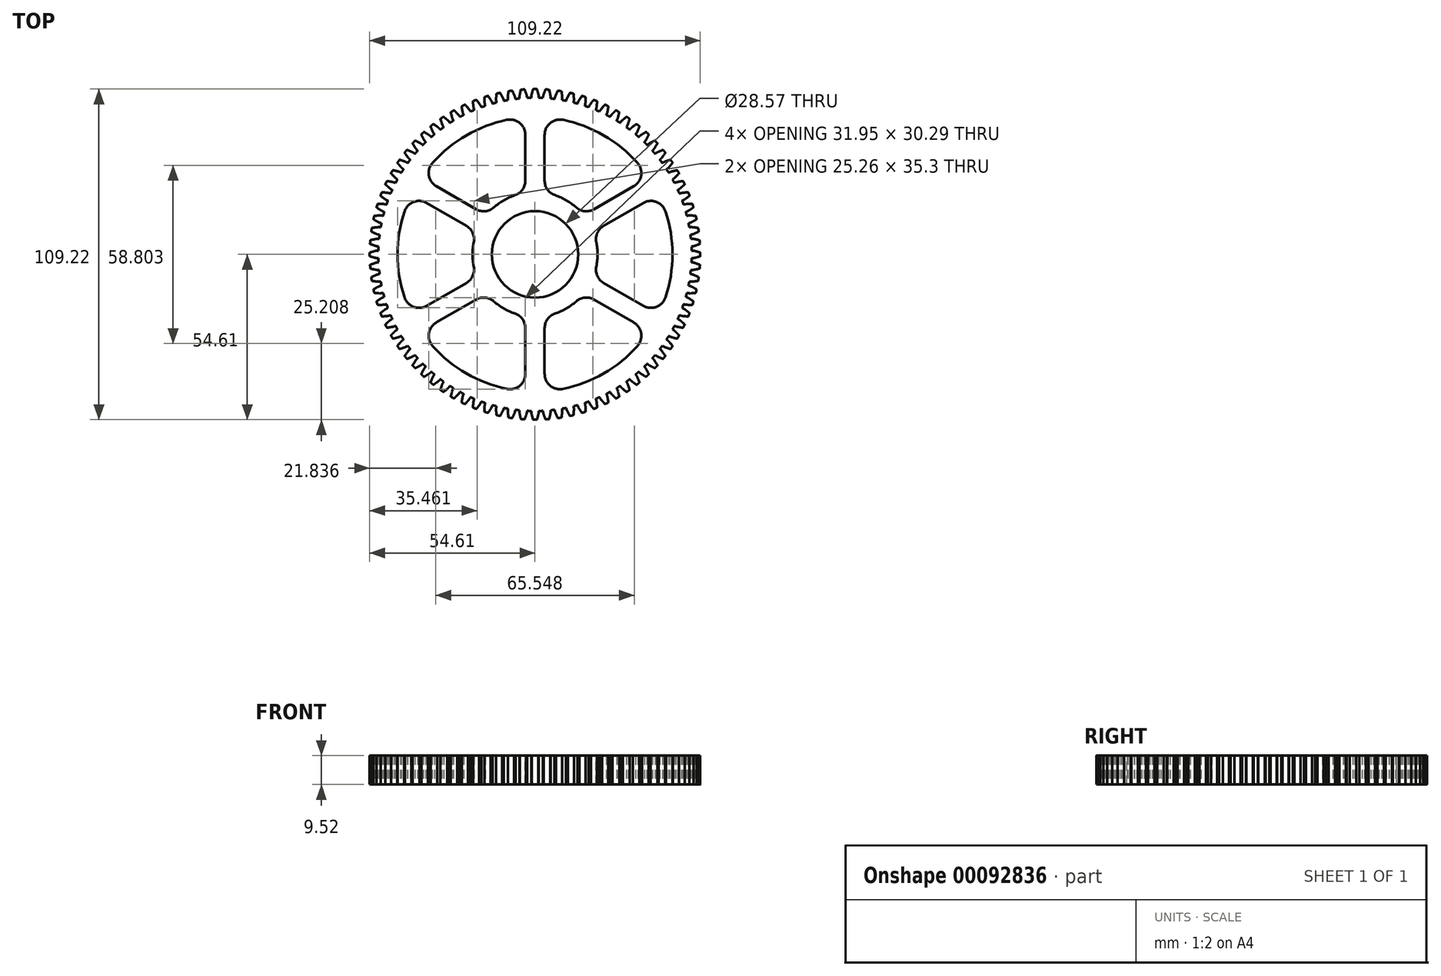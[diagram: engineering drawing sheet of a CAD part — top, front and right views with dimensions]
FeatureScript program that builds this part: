
annotation { "Feature Type Name" : "Feature", "Feature Type Description" : "" }
export const myFeature = defineFeature(function(context is Context, id is Id, definition is map)
    precondition{}
    {
        {
            var Q0;
            Q0=qCreatedBy(makeId("Top.planeOp"),FACE);
            var sketch = newSketch(context, id + "F0", { "sketchPlane" : qUnion([Q0])});
            skArc(sketch, "E0", {"start": v(1.25, 51.74) * mm, "mid": v(0, 51.75) * mm, "end": v(-1.25, 51.74) * mm});
            skArc(sketch, "E1", {"start": v(-1.25, -51.74) * mm, "mid": v(51.74, -1.25) * mm, "end": v(1.25, 51.74) * mm});
            skArc(sketch, "E2", {"start": v(-1.05, 53.12) * mm, "mid": v(-1.2, 52.43) * mm, "end": v(-1.25, 51.74) * mm});
            skArc(sketch, "E3", {"start": v(-0.67, 54.46) * mm, "mid": v(-0.86, 53.79) * mm, "end": v(-1.05, 53.12) * mm});
            skArc(sketch, "E4", {"start": v(-0.48, 54.6) * mm, "mid": v(-0.6, 54.57) * mm, "end": v(-0.67, 54.46) * mm});
            skArc(sketch, "E5", {"start": v(1.25, 51.74) * mm, "mid": v(1.2, 52.43) * mm, "end": v(1.05, 53.12) * mm});
            skArc(sketch, "E6", {"start": v(1.05, 53.12) * mm, "mid": v(0.86, 53.79) * mm, "end": v(0.67, 54.46) * mm});
            skArc(sketch, "E7", {"start": v(0.48, 54.6) * mm, "mid": v(0, 54.61) * mm, "end": v(-0.48, 54.6) * mm});
            skArc(sketch, "E8", {"start": v(0.67, 54.46) * mm, "mid": v(0.6, 54.57) * mm, "end": v(0.48, 54.6) * mm});
            skArc(sketch, "E9", {"start": v(-1.25, 51.74) * mm, "mid": v(-51.75, 0) * mm, "end": v(-1.25, -51.74) * mm});
            skSolve(sketch);
        }
        {
            var Q0;
            Q0=makeQuery(id+"F0.imprint","IMPRINT",FACE,{"disambiguationData":[TD([[makeQuery(id+"F0.imprint","IMPRINT",EDGE,{"derivedFrom":sQuery(id+"F0.wireOp",EDGE,"E0")}),1.0]])]});
            extrude(context, id + "F1", {"entities" : qUnion([Q0]), "depth" : 9.52 * mm, "symmetric" : true});
        }
        {
            var Q0;
            {var subQ0=sQuery(id+"F0.wireOp",EDGE,"E0");Q0=makeQuery(id+"F0.imprint","IMPRINT",FACE,{"disambiguationData":[TD([[makeQuery(id+"F0.imprint","IMPRINT",EDGE,{"derivedFrom":subQ0}),-1.0]])]});}
            var Q1;
            Q1=makeQuery(id+"F1.opExtrude","CAP_FACE",FACE,{"disambiguationData":[OSD([sQuery(id+"F0.wireOp",EDGE,"E0"),sQuery(id+"F0.wireOp",EDGE,"E1"),sQuery(id+"F0.wireOp",EDGE,"E9")])],"isStart":false});
            var Q2;
            Q2=makeQuery(id+"F1.opExtrude","CAP_FACE",FACE,{"disambiguationData":[OSD([sQuery(id+"F0.wireOp",EDGE,"E0"),sQuery(id+"F0.wireOp",EDGE,"E1"),sQuery(id+"F0.wireOp",EDGE,"E9")])],"isStart":true});
            extrude(context, id + "F2", {"entities" : qUnion([Q0]), "endBound" : BoundingType.UP_TO_SURFACE, "endBoundEntityFace" : qUnion([Q1]), "depth" : 25.4 * mm, "hasSecondDirection" : true, "secondDirectionBound" : BoundingType.UP_TO_SURFACE, "secondDirectionOppositeDirection" : true, "secondDirectionBoundEntityFace" : qUnion([Q2]), "secondDirectionDepth" : 25.4 * mm});
        }
        {
            var Q0;
            Q0=makeQuery(id+"F2.opExtrude","SWEPT_BODY",BODY,{"disambiguationData":[OSD([sQuery(id+"F0.wireOp",EDGE,"E0"),sQuery(id+"F0.wireOp",EDGE,"E2"),sQuery(id+"F0.wireOp",EDGE,"E3"),sQuery(id+"F0.wireOp",EDGE,"E4"),sQuery(id+"F0.wireOp",EDGE,"E5"),sQuery(id+"F0.wireOp",EDGE,"E6"),sQuery(id+"F0.wireOp",EDGE,"E7"),sQuery(id+"F0.wireOp",EDGE,"E8")])]});
            var Q1;
            Q1=makeQuery(id+"F1.opExtrude","SWEPT_FACE",FACE,{"disambiguationData":[OSD([sQuery(id+"F0.wireOp",EDGE,"E0"),sQuery(id+"F0.wireOp",EDGE,"E1"),sQuery(id+"F0.wireOp",EDGE,"E9")])]});
            circularPattern(context, id + "F3", {"operationType" : NewBodyOperationType.ADD, "entities" : qUnion([Q0]), "axis" : qUnion([Q1]), "angle" : 360 * degree, "instanceCount" : 84, "equalSpace" : true});
        }
        {
            var Q0;
            {var subQ0=sQuery(id+"F0.wireOp",EDGE,"E0");var subQ1=makeQuery(id+"F2.opExtrude","CAP_FACE",FACE,{"disambiguationData":[OSD([subQ0,sQuery(id+"F0.wireOp",EDGE,"E2"),sQuery(id+"F0.wireOp",EDGE,"E3"),sQuery(id+"F0.wireOp",EDGE,"E4"),sQuery(id+"F0.wireOp",EDGE,"E5"),sQuery(id+"F0.wireOp",EDGE,"E6"),sQuery(id+"F0.wireOp",EDGE,"E7"),sQuery(id+"F0.wireOp",EDGE,"E8")])],"isStart":false});Q0=makeQuery(id+"F3.boolean.opBoolean","MERGE",FACE,{"derivedFrom":[makeQuery(id+"F1.opExtrude","CAP_FACE",FACE,{"disambiguationData":[OSD([subQ0,sQuery(id+"F0.wireOp",EDGE,"E1"),sQuery(id+"F0.wireOp",EDGE,"E9")])],"isStart":false}),subQ1,makeQuery(id+"F3.opPattern","COPY",FACE,{"derivedFrom":subQ1,"instanceName":"1"}),makeQuery(id+"F3.opPattern","COPY",FACE,{"derivedFrom":subQ1,"instanceName":"2"}),makeQuery(id+"F3.opPattern","COPY",FACE,{"derivedFrom":subQ1,"instanceName":"3"}),makeQuery(id+"F3.opPattern","COPY",FACE,{"derivedFrom":subQ1,"instanceName":"4"}),makeQuery(id+"F3.opPattern","COPY",FACE,{"derivedFrom":subQ1,"instanceName":"5"}),makeQuery(id+"F3.opPattern","COPY",FACE,{"derivedFrom":subQ1,"instanceName":"6"}),makeQuery(id+"F3.opPattern","COPY",FACE,{"derivedFrom":subQ1,"instanceName":"7"}),makeQuery(id+"F3.opPattern","COPY",FACE,{"derivedFrom":subQ1,"instanceName":"8"}),makeQuery(id+"F3.opPattern","COPY",FACE,{"derivedFrom":subQ1,"instanceName":"9"}),makeQuery(id+"F3.opPattern","COPY",FACE,{"derivedFrom":subQ1,"instanceName":"10"}),makeQuery(id+"F3.opPattern","COPY",FACE,{"derivedFrom":subQ1,"instanceName":"11"}),makeQuery(id+"F3.opPattern","COPY",FACE,{"derivedFrom":subQ1,"instanceName":"12"}),makeQuery(id+"F3.opPattern","COPY",FACE,{"derivedFrom":subQ1,"instanceName":"13"}),makeQuery(id+"F3.opPattern","COPY",FACE,{"derivedFrom":subQ1,"instanceName":"14"}),makeQuery(id+"F3.opPattern","COPY",FACE,{"derivedFrom":subQ1,"instanceName":"15"}),makeQuery(id+"F3.opPattern","COPY",FACE,{"derivedFrom":subQ1,"instanceName":"16"}),makeQuery(id+"F3.opPattern","COPY",FACE,{"derivedFrom":subQ1,"instanceName":"17"}),makeQuery(id+"F3.opPattern","COPY",FACE,{"derivedFrom":subQ1,"instanceName":"18"}),makeQuery(id+"F3.opPattern","COPY",FACE,{"derivedFrom":subQ1,"instanceName":"19"}),makeQuery(id+"F3.opPattern","COPY",FACE,{"derivedFrom":subQ1,"instanceName":"20"}),makeQuery(id+"F3.opPattern","COPY",FACE,{"derivedFrom":subQ1,"instanceName":"21"}),makeQuery(id+"F3.opPattern","COPY",FACE,{"derivedFrom":subQ1,"instanceName":"22"}),makeQuery(id+"F3.opPattern","COPY",FACE,{"derivedFrom":subQ1,"instanceName":"23"}),makeQuery(id+"F3.opPattern","COPY",FACE,{"derivedFrom":subQ1,"instanceName":"24"}),makeQuery(id+"F3.opPattern","COPY",FACE,{"derivedFrom":subQ1,"instanceName":"25"}),makeQuery(id+"F3.opPattern","COPY",FACE,{"derivedFrom":subQ1,"instanceName":"26"}),makeQuery(id+"F3.opPattern","COPY",FACE,{"derivedFrom":subQ1,"instanceName":"27"}),makeQuery(id+"F3.opPattern","COPY",FACE,{"derivedFrom":subQ1,"instanceName":"28"}),makeQuery(id+"F3.opPattern","COPY",FACE,{"derivedFrom":subQ1,"instanceName":"29"}),makeQuery(id+"F3.opPattern","COPY",FACE,{"derivedFrom":subQ1,"instanceName":"30"}),makeQuery(id+"F3.opPattern","COPY",FACE,{"derivedFrom":subQ1,"instanceName":"31"}),makeQuery(id+"F3.opPattern","COPY",FACE,{"derivedFrom":subQ1,"instanceName":"32"}),makeQuery(id+"F3.opPattern","COPY",FACE,{"derivedFrom":subQ1,"instanceName":"33"}),makeQuery(id+"F3.opPattern","COPY",FACE,{"derivedFrom":subQ1,"instanceName":"34"}),makeQuery(id+"F3.opPattern","COPY",FACE,{"derivedFrom":subQ1,"instanceName":"35"}),makeQuery(id+"F3.opPattern","COPY",FACE,{"derivedFrom":subQ1,"instanceName":"36"}),makeQuery(id+"F3.opPattern","COPY",FACE,{"derivedFrom":subQ1,"instanceName":"37"}),makeQuery(id+"F3.opPattern","COPY",FACE,{"derivedFrom":subQ1,"instanceName":"38"}),makeQuery(id+"F3.opPattern","COPY",FACE,{"derivedFrom":subQ1,"instanceName":"39"}),makeQuery(id+"F3.opPattern","COPY",FACE,{"derivedFrom":subQ1,"instanceName":"40"}),makeQuery(id+"F3.opPattern","COPY",FACE,{"derivedFrom":subQ1,"instanceName":"41"}),makeQuery(id+"F3.opPattern","COPY",FACE,{"derivedFrom":subQ1,"instanceName":"42"}),makeQuery(id+"F3.opPattern","COPY",FACE,{"derivedFrom":subQ1,"instanceName":"43"}),makeQuery(id+"F3.opPattern","COPY",FACE,{"derivedFrom":subQ1,"instanceName":"44"}),makeQuery(id+"F3.opPattern","COPY",FACE,{"derivedFrom":subQ1,"instanceName":"45"}),makeQuery(id+"F3.opPattern","COPY",FACE,{"derivedFrom":subQ1,"instanceName":"46"}),makeQuery(id+"F3.opPattern","COPY",FACE,{"derivedFrom":subQ1,"instanceName":"47"}),makeQuery(id+"F3.opPattern","COPY",FACE,{"derivedFrom":subQ1,"instanceName":"48"}),makeQuery(id+"F3.opPattern","COPY",FACE,{"derivedFrom":subQ1,"instanceName":"49"}),makeQuery(id+"F3.opPattern","COPY",FACE,{"derivedFrom":subQ1,"instanceName":"50"}),makeQuery(id+"F3.opPattern","COPY",FACE,{"derivedFrom":subQ1,"instanceName":"51"}),makeQuery(id+"F3.opPattern","COPY",FACE,{"derivedFrom":subQ1,"instanceName":"52"}),makeQuery(id+"F3.opPattern","COPY",FACE,{"derivedFrom":subQ1,"instanceName":"53"}),makeQuery(id+"F3.opPattern","COPY",FACE,{"derivedFrom":subQ1,"instanceName":"54"}),makeQuery(id+"F3.opPattern","COPY",FACE,{"derivedFrom":subQ1,"instanceName":"55"}),makeQuery(id+"F3.opPattern","COPY",FACE,{"derivedFrom":subQ1,"instanceName":"56"}),makeQuery(id+"F3.opPattern","COPY",FACE,{"derivedFrom":subQ1,"instanceName":"57"}),makeQuery(id+"F3.opPattern","COPY",FACE,{"derivedFrom":subQ1,"instanceName":"58"}),makeQuery(id+"F3.opPattern","COPY",FACE,{"derivedFrom":subQ1,"instanceName":"59"}),makeQuery(id+"F3.opPattern","COPY",FACE,{"derivedFrom":subQ1,"instanceName":"60"}),makeQuery(id+"F3.opPattern","COPY",FACE,{"derivedFrom":subQ1,"instanceName":"61"}),makeQuery(id+"F3.opPattern","COPY",FACE,{"derivedFrom":subQ1,"instanceName":"62"}),makeQuery(id+"F3.opPattern","COPY",FACE,{"derivedFrom":subQ1,"instanceName":"63"}),makeQuery(id+"F3.opPattern","COPY",FACE,{"derivedFrom":subQ1,"instanceName":"64"}),makeQuery(id+"F3.opPattern","COPY",FACE,{"derivedFrom":subQ1,"instanceName":"65"}),makeQuery(id+"F3.opPattern","COPY",FACE,{"derivedFrom":subQ1,"instanceName":"66"}),makeQuery(id+"F3.opPattern","COPY",FACE,{"derivedFrom":subQ1,"instanceName":"67"}),makeQuery(id+"F3.opPattern","COPY",FACE,{"derivedFrom":subQ1,"instanceName":"68"}),makeQuery(id+"F3.opPattern","COPY",FACE,{"derivedFrom":subQ1,"instanceName":"69"}),makeQuery(id+"F3.opPattern","COPY",FACE,{"derivedFrom":subQ1,"instanceName":"70"}),makeQuery(id+"F3.opPattern","COPY",FACE,{"derivedFrom":subQ1,"instanceName":"71"}),makeQuery(id+"F3.opPattern","COPY",FACE,{"derivedFrom":subQ1,"instanceName":"72"}),makeQuery(id+"F3.opPattern","COPY",FACE,{"derivedFrom":subQ1,"instanceName":"73"}),makeQuery(id+"F3.opPattern","COPY",FACE,{"derivedFrom":subQ1,"instanceName":"74"}),makeQuery(id+"F3.opPattern","COPY",FACE,{"derivedFrom":subQ1,"instanceName":"75"}),makeQuery(id+"F3.opPattern","COPY",FACE,{"derivedFrom":subQ1,"instanceName":"76"}),makeQuery(id+"F3.opPattern","COPY",FACE,{"derivedFrom":subQ1,"instanceName":"77"}),makeQuery(id+"F3.opPattern","COPY",FACE,{"derivedFrom":subQ1,"instanceName":"78"}),makeQuery(id+"F3.opPattern","COPY",FACE,{"derivedFrom":subQ1,"instanceName":"79"}),makeQuery(id+"F3.opPattern","COPY",FACE,{"derivedFrom":subQ1,"instanceName":"80"}),makeQuery(id+"F3.opPattern","COPY",FACE,{"derivedFrom":subQ1,"instanceName":"81"}),makeQuery(id+"F3.opPattern","COPY",FACE,{"derivedFrom":subQ1,"instanceName":"82"}),makeQuery(id+"F3.opPattern","COPY",FACE,{"derivedFrom":subQ1,"instanceName":"83"})]});}
            var sketch = newSketch(context, id + "F4", { "sketchPlane" : qUnion([Q0])});
            skCircle(sketch, "E10", {"center": v(0, 0) * mm, "radius": 14.29 * mm});
            skSolve(sketch);
        }
        {
            var Q0;
            Q0=makeQuery(id+"F4.imprint","IMPRINT",FACE,{"disambiguationData":[TD([[makeQuery(id+"F4.imprint","IMPRINT",EDGE,{"derivedFrom":sQuery(id+"F4.wireOp",EDGE,"E10")}),1.0]])]});
            extrude(context, id + "F5", {"entities" : qUnion([Q0]), "operationType" : NewBodyOperationType.REMOVE, "endBound" : BoundingType.UP_TO_NEXT, "oppositeDirection" : true, "depth" : 25.4 * mm});
        }
        {
            var Q0;
            {var subQ0=sQuery(id+"F0.wireOp",EDGE,"E0");var subQ1=makeQuery(id+"F2.opExtrude","CAP_FACE",FACE,{"disambiguationData":[OSD([subQ0,sQuery(id+"F0.wireOp",EDGE,"E2"),sQuery(id+"F0.wireOp",EDGE,"E3"),sQuery(id+"F0.wireOp",EDGE,"E4"),sQuery(id+"F0.wireOp",EDGE,"E5"),sQuery(id+"F0.wireOp",EDGE,"E6"),sQuery(id+"F0.wireOp",EDGE,"E7"),sQuery(id+"F0.wireOp",EDGE,"E8")])],"isStart":false});Q0=makeQuery(id+"F3.boolean.opBoolean","MERGE",FACE,{"derivedFrom":[makeQuery(id+"F1.opExtrude","CAP_FACE",FACE,{"disambiguationData":[OSD([subQ0,sQuery(id+"F0.wireOp",EDGE,"E1"),sQuery(id+"F0.wireOp",EDGE,"E9")])],"isStart":false}),subQ1,makeQuery(id+"F3.opPattern","COPY",FACE,{"derivedFrom":subQ1,"instanceName":"1"}),makeQuery(id+"F3.opPattern","COPY",FACE,{"derivedFrom":subQ1,"instanceName":"2"}),makeQuery(id+"F3.opPattern","COPY",FACE,{"derivedFrom":subQ1,"instanceName":"3"}),makeQuery(id+"F3.opPattern","COPY",FACE,{"derivedFrom":subQ1,"instanceName":"4"}),makeQuery(id+"F3.opPattern","COPY",FACE,{"derivedFrom":subQ1,"instanceName":"5"}),makeQuery(id+"F3.opPattern","COPY",FACE,{"derivedFrom":subQ1,"instanceName":"6"}),makeQuery(id+"F3.opPattern","COPY",FACE,{"derivedFrom":subQ1,"instanceName":"7"}),makeQuery(id+"F3.opPattern","COPY",FACE,{"derivedFrom":subQ1,"instanceName":"8"}),makeQuery(id+"F3.opPattern","COPY",FACE,{"derivedFrom":subQ1,"instanceName":"9"}),makeQuery(id+"F3.opPattern","COPY",FACE,{"derivedFrom":subQ1,"instanceName":"10"}),makeQuery(id+"F3.opPattern","COPY",FACE,{"derivedFrom":subQ1,"instanceName":"11"}),makeQuery(id+"F3.opPattern","COPY",FACE,{"derivedFrom":subQ1,"instanceName":"12"}),makeQuery(id+"F3.opPattern","COPY",FACE,{"derivedFrom":subQ1,"instanceName":"13"}),makeQuery(id+"F3.opPattern","COPY",FACE,{"derivedFrom":subQ1,"instanceName":"14"}),makeQuery(id+"F3.opPattern","COPY",FACE,{"derivedFrom":subQ1,"instanceName":"15"}),makeQuery(id+"F3.opPattern","COPY",FACE,{"derivedFrom":subQ1,"instanceName":"16"}),makeQuery(id+"F3.opPattern","COPY",FACE,{"derivedFrom":subQ1,"instanceName":"17"}),makeQuery(id+"F3.opPattern","COPY",FACE,{"derivedFrom":subQ1,"instanceName":"18"}),makeQuery(id+"F3.opPattern","COPY",FACE,{"derivedFrom":subQ1,"instanceName":"19"}),makeQuery(id+"F3.opPattern","COPY",FACE,{"derivedFrom":subQ1,"instanceName":"20"}),makeQuery(id+"F3.opPattern","COPY",FACE,{"derivedFrom":subQ1,"instanceName":"21"}),makeQuery(id+"F3.opPattern","COPY",FACE,{"derivedFrom":subQ1,"instanceName":"22"}),makeQuery(id+"F3.opPattern","COPY",FACE,{"derivedFrom":subQ1,"instanceName":"23"}),makeQuery(id+"F3.opPattern","COPY",FACE,{"derivedFrom":subQ1,"instanceName":"24"}),makeQuery(id+"F3.opPattern","COPY",FACE,{"derivedFrom":subQ1,"instanceName":"25"}),makeQuery(id+"F3.opPattern","COPY",FACE,{"derivedFrom":subQ1,"instanceName":"26"}),makeQuery(id+"F3.opPattern","COPY",FACE,{"derivedFrom":subQ1,"instanceName":"27"}),makeQuery(id+"F3.opPattern","COPY",FACE,{"derivedFrom":subQ1,"instanceName":"28"}),makeQuery(id+"F3.opPattern","COPY",FACE,{"derivedFrom":subQ1,"instanceName":"29"}),makeQuery(id+"F3.opPattern","COPY",FACE,{"derivedFrom":subQ1,"instanceName":"30"}),makeQuery(id+"F3.opPattern","COPY",FACE,{"derivedFrom":subQ1,"instanceName":"31"}),makeQuery(id+"F3.opPattern","COPY",FACE,{"derivedFrom":subQ1,"instanceName":"32"}),makeQuery(id+"F3.opPattern","COPY",FACE,{"derivedFrom":subQ1,"instanceName":"33"}),makeQuery(id+"F3.opPattern","COPY",FACE,{"derivedFrom":subQ1,"instanceName":"34"}),makeQuery(id+"F3.opPattern","COPY",FACE,{"derivedFrom":subQ1,"instanceName":"35"}),makeQuery(id+"F3.opPattern","COPY",FACE,{"derivedFrom":subQ1,"instanceName":"36"}),makeQuery(id+"F3.opPattern","COPY",FACE,{"derivedFrom":subQ1,"instanceName":"37"}),makeQuery(id+"F3.opPattern","COPY",FACE,{"derivedFrom":subQ1,"instanceName":"38"}),makeQuery(id+"F3.opPattern","COPY",FACE,{"derivedFrom":subQ1,"instanceName":"39"}),makeQuery(id+"F3.opPattern","COPY",FACE,{"derivedFrom":subQ1,"instanceName":"40"}),makeQuery(id+"F3.opPattern","COPY",FACE,{"derivedFrom":subQ1,"instanceName":"41"}),makeQuery(id+"F3.opPattern","COPY",FACE,{"derivedFrom":subQ1,"instanceName":"42"}),makeQuery(id+"F3.opPattern","COPY",FACE,{"derivedFrom":subQ1,"instanceName":"43"}),makeQuery(id+"F3.opPattern","COPY",FACE,{"derivedFrom":subQ1,"instanceName":"44"}),makeQuery(id+"F3.opPattern","COPY",FACE,{"derivedFrom":subQ1,"instanceName":"45"}),makeQuery(id+"F3.opPattern","COPY",FACE,{"derivedFrom":subQ1,"instanceName":"46"}),makeQuery(id+"F3.opPattern","COPY",FACE,{"derivedFrom":subQ1,"instanceName":"47"}),makeQuery(id+"F3.opPattern","COPY",FACE,{"derivedFrom":subQ1,"instanceName":"48"}),makeQuery(id+"F3.opPattern","COPY",FACE,{"derivedFrom":subQ1,"instanceName":"49"}),makeQuery(id+"F3.opPattern","COPY",FACE,{"derivedFrom":subQ1,"instanceName":"50"}),makeQuery(id+"F3.opPattern","COPY",FACE,{"derivedFrom":subQ1,"instanceName":"51"}),makeQuery(id+"F3.opPattern","COPY",FACE,{"derivedFrom":subQ1,"instanceName":"52"}),makeQuery(id+"F3.opPattern","COPY",FACE,{"derivedFrom":subQ1,"instanceName":"53"}),makeQuery(id+"F3.opPattern","COPY",FACE,{"derivedFrom":subQ1,"instanceName":"54"}),makeQuery(id+"F3.opPattern","COPY",FACE,{"derivedFrom":subQ1,"instanceName":"55"}),makeQuery(id+"F3.opPattern","COPY",FACE,{"derivedFrom":subQ1,"instanceName":"56"}),makeQuery(id+"F3.opPattern","COPY",FACE,{"derivedFrom":subQ1,"instanceName":"57"}),makeQuery(id+"F3.opPattern","COPY",FACE,{"derivedFrom":subQ1,"instanceName":"58"}),makeQuery(id+"F3.opPattern","COPY",FACE,{"derivedFrom":subQ1,"instanceName":"59"}),makeQuery(id+"F3.opPattern","COPY",FACE,{"derivedFrom":subQ1,"instanceName":"60"}),makeQuery(id+"F3.opPattern","COPY",FACE,{"derivedFrom":subQ1,"instanceName":"61"}),makeQuery(id+"F3.opPattern","COPY",FACE,{"derivedFrom":subQ1,"instanceName":"62"}),makeQuery(id+"F3.opPattern","COPY",FACE,{"derivedFrom":subQ1,"instanceName":"63"}),makeQuery(id+"F3.opPattern","COPY",FACE,{"derivedFrom":subQ1,"instanceName":"64"}),makeQuery(id+"F3.opPattern","COPY",FACE,{"derivedFrom":subQ1,"instanceName":"65"}),makeQuery(id+"F3.opPattern","COPY",FACE,{"derivedFrom":subQ1,"instanceName":"66"}),makeQuery(id+"F3.opPattern","COPY",FACE,{"derivedFrom":subQ1,"instanceName":"67"}),makeQuery(id+"F3.opPattern","COPY",FACE,{"derivedFrom":subQ1,"instanceName":"68"}),makeQuery(id+"F3.opPattern","COPY",FACE,{"derivedFrom":subQ1,"instanceName":"69"}),makeQuery(id+"F3.opPattern","COPY",FACE,{"derivedFrom":subQ1,"instanceName":"70"}),makeQuery(id+"F3.opPattern","COPY",FACE,{"derivedFrom":subQ1,"instanceName":"71"}),makeQuery(id+"F3.opPattern","COPY",FACE,{"derivedFrom":subQ1,"instanceName":"72"}),makeQuery(id+"F3.opPattern","COPY",FACE,{"derivedFrom":subQ1,"instanceName":"73"}),makeQuery(id+"F3.opPattern","COPY",FACE,{"derivedFrom":subQ1,"instanceName":"74"}),makeQuery(id+"F3.opPattern","COPY",FACE,{"derivedFrom":subQ1,"instanceName":"75"}),makeQuery(id+"F3.opPattern","COPY",FACE,{"derivedFrom":subQ1,"instanceName":"76"}),makeQuery(id+"F3.opPattern","COPY",FACE,{"derivedFrom":subQ1,"instanceName":"77"}),makeQuery(id+"F3.opPattern","COPY",FACE,{"derivedFrom":subQ1,"instanceName":"78"}),makeQuery(id+"F3.opPattern","COPY",FACE,{"derivedFrom":subQ1,"instanceName":"79"}),makeQuery(id+"F3.opPattern","COPY",FACE,{"derivedFrom":subQ1,"instanceName":"80"}),makeQuery(id+"F3.opPattern","COPY",FACE,{"derivedFrom":subQ1,"instanceName":"81"}),makeQuery(id+"F3.opPattern","COPY",FACE,{"derivedFrom":subQ1,"instanceName":"82"}),makeQuery(id+"F3.opPattern","COPY",FACE,{"derivedFrom":subQ1,"instanceName":"83"})]});}
            var sketch = newSketch(context, id + "F6", { "sketchPlane" : qUnion([Q0])});
            skArc(sketch, "E11", {"start": v(0, 20.64) * mm, "mid": v(-10.32, 17.87) * mm, "end": v(-17.87, 10.32) * mm});
            skArc(sketch, "E12", {"start": v(0, 45.4) * mm, "mid": v(-22.7, 39.32) * mm, "end": v(-39.32, 22.7) * mm});
            skLineSegment(sketch, "E13", {"start": v(0, 20.64) * mm, "end": v(0, 45.4) * mm, "construction": true});
            skLineSegment(sketch, "E14", {"start": v(-17.87, 10.32) * mm, "end": v(-39.32, 22.7) * mm, "construction": true});
            skLineSegment(sketch, "E15.0", {"start": v(-16.07, 12.95) * mm, "end": v(-37.64, 25.4) * mm});
            skLineSegment(sketch, "E16.0", {"start": v(-3.18, 20.4) * mm, "end": v(-3.18, 45.3) * mm});
            skSolve(sketch);
        }
        {
            var Q0;
            {var subQ0=sQuery(id+"F6.wireOp",EDGE,"E15.0");Q0=makeQuery(id+"F6.imprint","IMPRINT",FACE,{"disambiguationData":[TD([[makeQuery(id+"F6.imprint","IMPRINT",EDGE,{"derivedFrom":subQ0}),-1.0]])]});}
            var Q1;
            {var subQ0=sQuery(id+"F0.wireOp",EDGE,"E0");var subQ1=makeQuery(id+"F2.opExtrude","CAP_FACE",FACE,{"disambiguationData":[OSD([subQ0,sQuery(id+"F0.wireOp",EDGE,"E2"),sQuery(id+"F0.wireOp",EDGE,"E3"),sQuery(id+"F0.wireOp",EDGE,"E4"),sQuery(id+"F0.wireOp",EDGE,"E5"),sQuery(id+"F0.wireOp",EDGE,"E6"),sQuery(id+"F0.wireOp",EDGE,"E7"),sQuery(id+"F0.wireOp",EDGE,"E8")])],"isStart":true});Q1=makeQuery(id+"F3.boolean.opBoolean","MERGE",FACE,{"derivedFrom":[makeQuery(id+"F1.opExtrude","CAP_FACE",FACE,{"disambiguationData":[OSD([subQ0,sQuery(id+"F0.wireOp",EDGE,"E1"),sQuery(id+"F0.wireOp",EDGE,"E9")])],"isStart":true}),subQ1,makeQuery(id+"F3.opPattern","COPY",FACE,{"derivedFrom":subQ1,"instanceName":"1"}),makeQuery(id+"F3.opPattern","COPY",FACE,{"derivedFrom":subQ1,"instanceName":"2"}),makeQuery(id+"F3.opPattern","COPY",FACE,{"derivedFrom":subQ1,"instanceName":"3"}),makeQuery(id+"F3.opPattern","COPY",FACE,{"derivedFrom":subQ1,"instanceName":"4"}),makeQuery(id+"F3.opPattern","COPY",FACE,{"derivedFrom":subQ1,"instanceName":"5"}),makeQuery(id+"F3.opPattern","COPY",FACE,{"derivedFrom":subQ1,"instanceName":"6"}),makeQuery(id+"F3.opPattern","COPY",FACE,{"derivedFrom":subQ1,"instanceName":"7"}),makeQuery(id+"F3.opPattern","COPY",FACE,{"derivedFrom":subQ1,"instanceName":"8"}),makeQuery(id+"F3.opPattern","COPY",FACE,{"derivedFrom":subQ1,"instanceName":"9"}),makeQuery(id+"F3.opPattern","COPY",FACE,{"derivedFrom":subQ1,"instanceName":"10"}),makeQuery(id+"F3.opPattern","COPY",FACE,{"derivedFrom":subQ1,"instanceName":"11"}),makeQuery(id+"F3.opPattern","COPY",FACE,{"derivedFrom":subQ1,"instanceName":"12"}),makeQuery(id+"F3.opPattern","COPY",FACE,{"derivedFrom":subQ1,"instanceName":"13"}),makeQuery(id+"F3.opPattern","COPY",FACE,{"derivedFrom":subQ1,"instanceName":"14"}),makeQuery(id+"F3.opPattern","COPY",FACE,{"derivedFrom":subQ1,"instanceName":"15"}),makeQuery(id+"F3.opPattern","COPY",FACE,{"derivedFrom":subQ1,"instanceName":"16"}),makeQuery(id+"F3.opPattern","COPY",FACE,{"derivedFrom":subQ1,"instanceName":"17"}),makeQuery(id+"F3.opPattern","COPY",FACE,{"derivedFrom":subQ1,"instanceName":"18"}),makeQuery(id+"F3.opPattern","COPY",FACE,{"derivedFrom":subQ1,"instanceName":"19"}),makeQuery(id+"F3.opPattern","COPY",FACE,{"derivedFrom":subQ1,"instanceName":"20"}),makeQuery(id+"F3.opPattern","COPY",FACE,{"derivedFrom":subQ1,"instanceName":"21"}),makeQuery(id+"F3.opPattern","COPY",FACE,{"derivedFrom":subQ1,"instanceName":"22"}),makeQuery(id+"F3.opPattern","COPY",FACE,{"derivedFrom":subQ1,"instanceName":"23"}),makeQuery(id+"F3.opPattern","COPY",FACE,{"derivedFrom":subQ1,"instanceName":"24"}),makeQuery(id+"F3.opPattern","COPY",FACE,{"derivedFrom":subQ1,"instanceName":"25"}),makeQuery(id+"F3.opPattern","COPY",FACE,{"derivedFrom":subQ1,"instanceName":"26"}),makeQuery(id+"F3.opPattern","COPY",FACE,{"derivedFrom":subQ1,"instanceName":"27"}),makeQuery(id+"F3.opPattern","COPY",FACE,{"derivedFrom":subQ1,"instanceName":"28"}),makeQuery(id+"F3.opPattern","COPY",FACE,{"derivedFrom":subQ1,"instanceName":"29"}),makeQuery(id+"F3.opPattern","COPY",FACE,{"derivedFrom":subQ1,"instanceName":"30"}),makeQuery(id+"F3.opPattern","COPY",FACE,{"derivedFrom":subQ1,"instanceName":"31"}),makeQuery(id+"F3.opPattern","COPY",FACE,{"derivedFrom":subQ1,"instanceName":"32"}),makeQuery(id+"F3.opPattern","COPY",FACE,{"derivedFrom":subQ1,"instanceName":"33"}),makeQuery(id+"F3.opPattern","COPY",FACE,{"derivedFrom":subQ1,"instanceName":"34"}),makeQuery(id+"F3.opPattern","COPY",FACE,{"derivedFrom":subQ1,"instanceName":"35"}),makeQuery(id+"F3.opPattern","COPY",FACE,{"derivedFrom":subQ1,"instanceName":"36"}),makeQuery(id+"F3.opPattern","COPY",FACE,{"derivedFrom":subQ1,"instanceName":"37"}),makeQuery(id+"F3.opPattern","COPY",FACE,{"derivedFrom":subQ1,"instanceName":"38"}),makeQuery(id+"F3.opPattern","COPY",FACE,{"derivedFrom":subQ1,"instanceName":"39"}),makeQuery(id+"F3.opPattern","COPY",FACE,{"derivedFrom":subQ1,"instanceName":"40"}),makeQuery(id+"F3.opPattern","COPY",FACE,{"derivedFrom":subQ1,"instanceName":"41"}),makeQuery(id+"F3.opPattern","COPY",FACE,{"derivedFrom":subQ1,"instanceName":"42"}),makeQuery(id+"F3.opPattern","COPY",FACE,{"derivedFrom":subQ1,"instanceName":"43"}),makeQuery(id+"F3.opPattern","COPY",FACE,{"derivedFrom":subQ1,"instanceName":"44"}),makeQuery(id+"F3.opPattern","COPY",FACE,{"derivedFrom":subQ1,"instanceName":"45"}),makeQuery(id+"F3.opPattern","COPY",FACE,{"derivedFrom":subQ1,"instanceName":"46"}),makeQuery(id+"F3.opPattern","COPY",FACE,{"derivedFrom":subQ1,"instanceName":"47"}),makeQuery(id+"F3.opPattern","COPY",FACE,{"derivedFrom":subQ1,"instanceName":"48"}),makeQuery(id+"F3.opPattern","COPY",FACE,{"derivedFrom":subQ1,"instanceName":"49"}),makeQuery(id+"F3.opPattern","COPY",FACE,{"derivedFrom":subQ1,"instanceName":"50"}),makeQuery(id+"F3.opPattern","COPY",FACE,{"derivedFrom":subQ1,"instanceName":"51"}),makeQuery(id+"F3.opPattern","COPY",FACE,{"derivedFrom":subQ1,"instanceName":"52"}),makeQuery(id+"F3.opPattern","COPY",FACE,{"derivedFrom":subQ1,"instanceName":"53"}),makeQuery(id+"F3.opPattern","COPY",FACE,{"derivedFrom":subQ1,"instanceName":"54"}),makeQuery(id+"F3.opPattern","COPY",FACE,{"derivedFrom":subQ1,"instanceName":"55"}),makeQuery(id+"F3.opPattern","COPY",FACE,{"derivedFrom":subQ1,"instanceName":"56"}),makeQuery(id+"F3.opPattern","COPY",FACE,{"derivedFrom":subQ1,"instanceName":"57"}),makeQuery(id+"F3.opPattern","COPY",FACE,{"derivedFrom":subQ1,"instanceName":"58"}),makeQuery(id+"F3.opPattern","COPY",FACE,{"derivedFrom":subQ1,"instanceName":"59"}),makeQuery(id+"F3.opPattern","COPY",FACE,{"derivedFrom":subQ1,"instanceName":"60"}),makeQuery(id+"F3.opPattern","COPY",FACE,{"derivedFrom":subQ1,"instanceName":"61"}),makeQuery(id+"F3.opPattern","COPY",FACE,{"derivedFrom":subQ1,"instanceName":"62"}),makeQuery(id+"F3.opPattern","COPY",FACE,{"derivedFrom":subQ1,"instanceName":"63"}),makeQuery(id+"F3.opPattern","COPY",FACE,{"derivedFrom":subQ1,"instanceName":"64"}),makeQuery(id+"F3.opPattern","COPY",FACE,{"derivedFrom":subQ1,"instanceName":"65"}),makeQuery(id+"F3.opPattern","COPY",FACE,{"derivedFrom":subQ1,"instanceName":"66"}),makeQuery(id+"F3.opPattern","COPY",FACE,{"derivedFrom":subQ1,"instanceName":"67"}),makeQuery(id+"F3.opPattern","COPY",FACE,{"derivedFrom":subQ1,"instanceName":"68"}),makeQuery(id+"F3.opPattern","COPY",FACE,{"derivedFrom":subQ1,"instanceName":"69"}),makeQuery(id+"F3.opPattern","COPY",FACE,{"derivedFrom":subQ1,"instanceName":"70"}),makeQuery(id+"F3.opPattern","COPY",FACE,{"derivedFrom":subQ1,"instanceName":"71"}),makeQuery(id+"F3.opPattern","COPY",FACE,{"derivedFrom":subQ1,"instanceName":"72"}),makeQuery(id+"F3.opPattern","COPY",FACE,{"derivedFrom":subQ1,"instanceName":"73"}),makeQuery(id+"F3.opPattern","COPY",FACE,{"derivedFrom":subQ1,"instanceName":"74"}),makeQuery(id+"F3.opPattern","COPY",FACE,{"derivedFrom":subQ1,"instanceName":"75"}),makeQuery(id+"F3.opPattern","COPY",FACE,{"derivedFrom":subQ1,"instanceName":"76"}),makeQuery(id+"F3.opPattern","COPY",FACE,{"derivedFrom":subQ1,"instanceName":"77"}),makeQuery(id+"F3.opPattern","COPY",FACE,{"derivedFrom":subQ1,"instanceName":"78"}),makeQuery(id+"F3.opPattern","COPY",FACE,{"derivedFrom":subQ1,"instanceName":"79"}),makeQuery(id+"F3.opPattern","COPY",FACE,{"derivedFrom":subQ1,"instanceName":"80"}),makeQuery(id+"F3.opPattern","COPY",FACE,{"derivedFrom":subQ1,"instanceName":"81"}),makeQuery(id+"F3.opPattern","COPY",FACE,{"derivedFrom":subQ1,"instanceName":"82"}),makeQuery(id+"F3.opPattern","COPY",FACE,{"derivedFrom":subQ1,"instanceName":"83"})]});}
            extrude(context, id + "F7", {"entities" : qUnion([Q0]), "endBound" : BoundingType.UP_TO_SURFACE, "oppositeDirection" : true, "endBoundEntityFace" : qUnion([Q1]), "depth" : 25.4 * mm});
        }
        {
            var Q0;
            Q0=makeQuery(id+"F7.opExtrude","SWEPT_EDGE",EDGE,{"disambiguationData":[OSD([sQuery(id+"F6.wireOp",EDGE,"E12"),sQuery(id+"F6.wireOp",EDGE,"E16.0")])]});
            var Q1;
            Q1=makeQuery(id+"F7.opExtrude","SWEPT_EDGE",EDGE,{"disambiguationData":[OSD([sQuery(id+"F6.wireOp",EDGE,"E11"),sQuery(id+"F6.wireOp",EDGE,"E16.0")])]});
            var Q2;
            Q2=makeQuery(id+"F7.opExtrude","SWEPT_EDGE",EDGE,{"disambiguationData":[OSD([sQuery(id+"F6.wireOp",EDGE,"E11"),sQuery(id+"F6.wireOp",EDGE,"E15.0")])]});
            var Q3;
            Q3=makeQuery(id+"F7.opExtrude","SWEPT_EDGE",EDGE,{"disambiguationData":[OSD([sQuery(id+"F6.wireOp",EDGE,"E12"),sQuery(id+"F6.wireOp",EDGE,"E15.0")])]});
            fillet(context, id + "F8", {"entities" : qUnion([Q0, Q1, Q2, Q3]), "radius" : 5.08 * mm, "tangentPropagation" : true, "allowEdgeOverflow" : false});
        }
        {
            var Q0;
            Q0=makeQuery(id+"F7.opExtrude","SWEPT_BODY",BODY,{"disambiguationData":[OSD([sQuery(id+"F6.wireOp",EDGE,"E11"),sQuery(id+"F6.wireOp",EDGE,"E12"),sQuery(id+"F6.wireOp",EDGE,"E15.0"),sQuery(id+"F6.wireOp",EDGE,"E16.0")])]});
            var Q1;
            Q1=makeQuery(id+"F5.boolean.opBoolean","COPY",FACE,{"derivedFrom":makeQuery(id+"F5.opExtrude","SWEPT_FACE",FACE,{"disambiguationData":[OSD([sQuery(id+"F4.wireOp",EDGE,"E10")])]})});
            circularPattern(context, id + "F9", {"operationType" : NewBodyOperationType.REMOVE, "entities" : qUnion([Q0]), "axis" : qUnion([Q1]), "angle" : 360 * degree, "instanceCount" : 6, "equalSpace" : true});
        }
    });
